# Revit family: basel_led__m1500_-_5280lm__pc_tropal_r___bruchsicher__840_4000k__zone_2_22_raumstrahlend_5256803484-e_40aa
name_source: partatom
category: Lighting Fixtures
units: mm (PartAtom-declared; Revit-internal decimal feet)

## family parameters
Cut with Voids When Loaded = No
Host = Face
Light Source = No
Part Type = Normal
Room Calculation Point = No
Round Connector Dimension = Use Diameter
Shared = No

## types (1)
- BASEL LED, m1500 - 5280lm, PC Tropal® (bruchsicher), 840/4000K, Zone 2/22 raumstrahlend (1 x LED Stripe, 5280 lm, 27 W, 840/4000K)
    Apparent Load = 30 VA
    Approval mark = CE, ENEC
    CIE Flux Codes = 56 85 96 98 98
    Color Rendering = 1B/80..89
    Color Temperature = 840/4000K
    Default Elevation = 1800 mm
    Description = Explosion-proof surface mounted ceiling luminaire made of polymer with LED lamps. Useable in industrial applications with explosive atmospheres according to zone 2, 22. Designed according to the applicable European Directives. Weather-proof and UV-resistant luminaire housing made of fibreglass-reinforced polymer, similar to RAL 9010. Useable for indoor and outdoor areas according to protection rating IP 65. Thermally separated lamp chamber and driver chamber. Short sealing system consisting of age-resistant, form-retaining silicone/synthetic rubber. Reflector tube that can be swivelled, made of PC Tropal® (fracture proof) with internal aluminium reflector (MIRO-SILVER®). Reflector tube can be locked in steps of 10°. Luminaire ready for mounting and installation. Built-in driver 230 V AC/DC. Two access covers, two cable glands on face side M20 and 5 x 1.5 mm² through wiring. Single or row mounting. Ceiling installation using two special polymer mounting clamps, variable mounting distance.


Length: 1551 mm
Width: 107 mm
Height: 153 mm
Weight: 3.6 kg

LOR: 97.7 %
    Height = 153 mm
    Lamp = 1 x LED Stripe
    Lamp Light Flux = 5280 lm
    Lamp Power = 27 W
    Lamp count = 1
    Length = 1551 mm
    Lifetime = 60000 h
    Luminous efficacy = 172 lm/W
    Manufacturer = NORKA
    ModVariant = No
    Model = 5256803484-E
    Mounting Place = Ceiling, Wall
    Mounting Type = Surface mounted, Rail mounted
    Number of Poles = 1
    OnlyDefault = Yes
    Power Factor = 1
    Product Name = BASEL LED, m1500 - 5280lm, PC Tropal® (bruchsicher), 840/4000K, Zone 2/22 raumstrahlend
    Product group = Explosion proof luminaire fixed mounting
    ProductGroupID = 5
    Protection Class = Protection class II
    Protection Degree = IP 65
    RLX_Detail_Level = 1
    RlxData = <blob elided: 252081 chars, md5=a7ed2c94>
    Socket = socket
    Standby Power = 0 W
    System Light Flux = 5159 lm
    System Power = 30 W
    Type Comments = Product without accessories
    Type Image = basel-led-transopal.jpg
    URL = http://relux.com
    VarID = ---
    Voltage = 0 V
    Weight = 0.00 kg
    Width = 107 mm

## geometry (parser evidence)
native form markers: Sweep x13
no freeform markers — native parametric forms only
